# Revit family: 11Landscaping_Bike-Racks-Shelters_Saris-Infrastructure_Bike-Wash-Station
name_source: partatom
category: Site
units: mm (PartAtom-declared; Revit-internal decimal feet)

## family parameters
Always vertical = Yes
Cut with Voids When Loaded = No
OmniClass Number = 23.40.10.11
Part Type = Normal
Round Connector Dimension = Use Diameter
Shared = No
Work Plane-Based = No

## types (1)
- Bike Wash Station, Black Powder Coat w/ e-Coat
    Date Updated = 2025/03/14
    Default Elevation = 0.00"
    Description = Bike Wash Station, Black Powder Coat w/ eCoat - 26702BLK
    Height = 49.60"
    Length = 17.70"
    Manufacturer = Saris Infrastructure
    Model = 26702BLK
    Product Documentation Link = https://cdn.shopify.com
    Product Material = Saris Infrastructure - Mild Steel - Powder Coat - Black with e-coat
    Product Page URL = https://sarisinfrastructure.com
    Product Specifications = • Universal bike mounting - hang by seat or top tube to keep bike stable when in use.  • Includes four cleaning brushes for various components,
 attached by braided stainless steel cable to prevent theft.
 •Coiled hose with adjustable nozzle provides strong cleaning
 power.
 • System can be plumbed from underneath or a side access can
 be connected to a standard garden hose.
    Product data url = https://bimobject.com
    URL = https://www.sarisinfrastructure.com
    Version = 1
    Warranty = 2 years
    Weight = 0.00 lbf
    Width = 10.20"

## geometry (parser evidence)
native form markers: Extrusion x1, Sweep x3
no freeform markers — native parametric forms only
